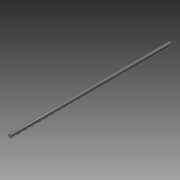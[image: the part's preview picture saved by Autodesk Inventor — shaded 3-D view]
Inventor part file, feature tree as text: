
AUTODESK INVENTOR PART (.ipt)
format: ipt  version: 2014 (Build 180170000, 170)  size: 82,944 bytes
history: native  units: in
note: dims shown in document units (in); Inventor stores cm internally (conversion verified against a paired STEP export)
features: extrude x1, other x1, thread x1, imported_body x1
ambient origin geometry x8: Origin, YZ Plane, XZ Plane, XY Plane, X Axis, Y Axis, Z Axis, Center Point
bodies: Body1 (feature_tree)
feature tree (4):
  extrude  "Extrude1"  Depth=1.0in TaperAngle=0.0deg
  other  "Ametek-BFWFSR-043-0197-18_screw.ipt1"
  thread  "Thread1"  [1 undecoded]
  imported_body  "Base1"
note: 1 required parameter value undecoded (feature->parameter linkage not recoverable at this tier; creation-order binding heuristic only, values carry confidence <= 0.55)
